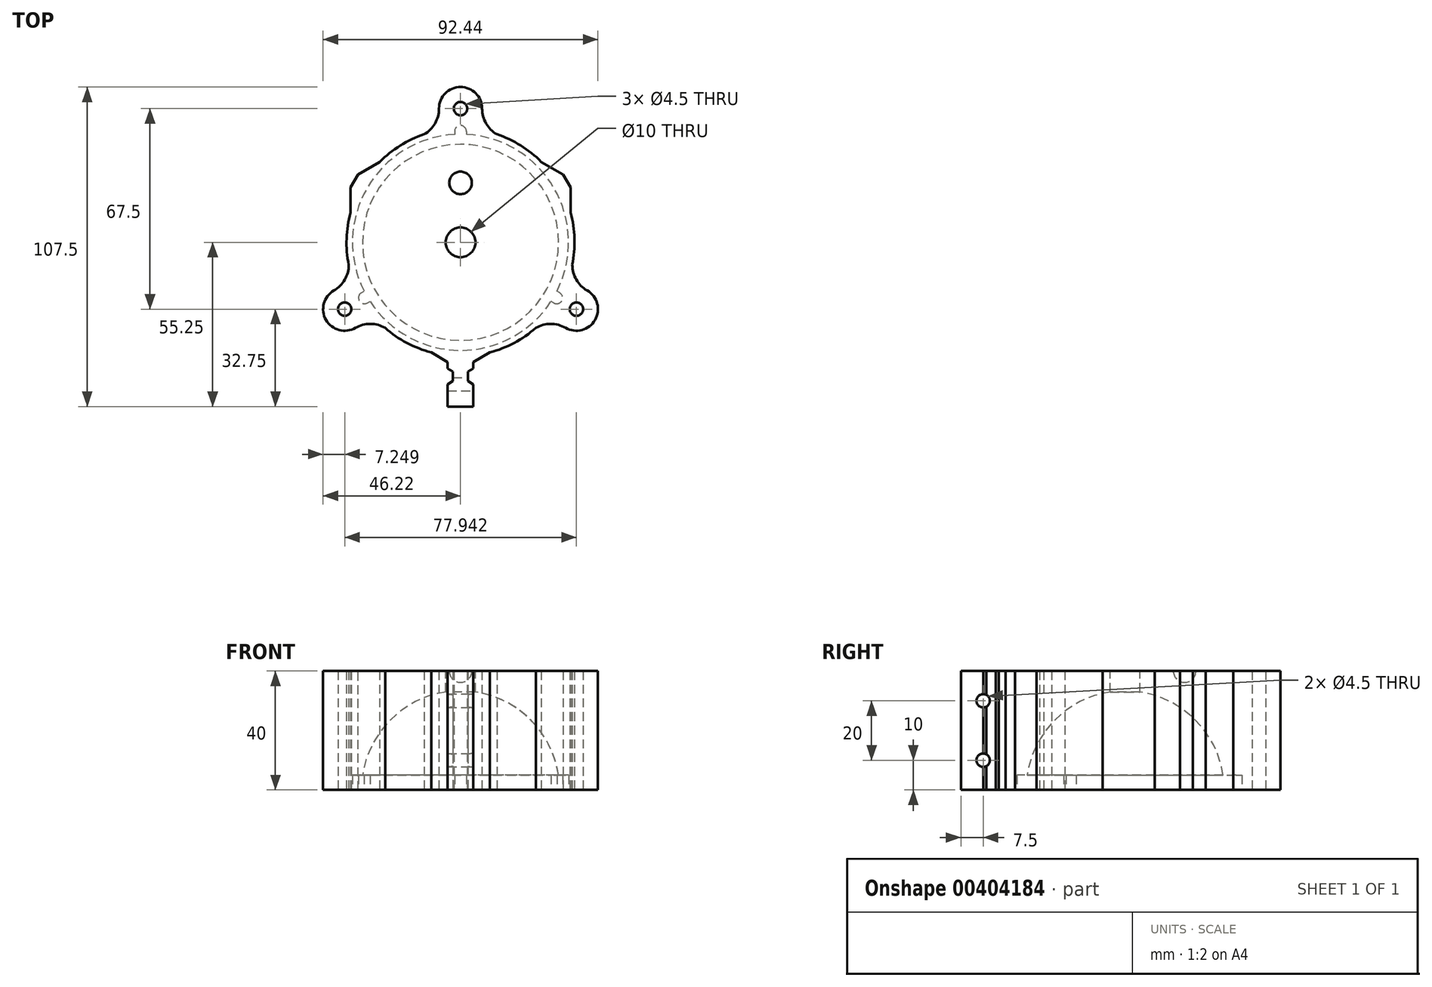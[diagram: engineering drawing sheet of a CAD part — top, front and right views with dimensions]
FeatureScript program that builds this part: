
annotation { "Feature Type Name" : "Feature", "Feature Type Description" : "" }
export const myFeature = defineFeature(function(context is Context, id is Id, definition is map)
    precondition{}
    {
        {
            var Q0;
            Q0=qCreatedBy(makeId("Top.planeOp"),FACE);
            var sketch = newSketch(context, id + "F0", { "sketchPlane" : qUnion([Q0])});
            skCircle(sketch, "E0", {"center": v(0, 0) * mm, "radius": 33.35 * mm});
            skCircle(sketch, "E1", {"center": v(0, 45) * mm, "radius": 2.25 * mm});
            skCircle(sketch, "E2", {"center": v(38.97, -22.5) * mm, "radius": 2.25 * mm});
            skCircle(sketch, "E3", {"center": v(-38.97, -22.5) * mm, "radius": 2.25 * mm});
            skArc(sketch, "E4", {"start": v(-25.35, -28.78) * mm, "mid": v(0, -38.35) * mm, "end": v(25.35, -28.78) * mm});
            skLineSegment(sketch, "E5", {"start": v(0, 0) * mm, "end": v(38.97, -22.5) * mm, "construction": true});
            skLineSegment(sketch, "E6", {"start": v(-38.97, -22.5) * mm, "end": v(0, 0) * mm, "construction": true});
            skArc(sketch, "E7", {"start": v(7.25, 45) * mm, "mid": v(0, 52.25) * mm, "end": v(-7.25, 45) * mm});
            skArc(sketch, "E8.1.0", {"start": v(-42.6, -16.22) * mm, "mid": v(-45.25, -26.12) * mm, "end": v(-35.35, -28.78) * mm});
            skArc(sketch, "E8.2.0", {"start": v(35.35, -28.78) * mm, "mid": v(45.25, -26.12) * mm, "end": v(42.6, -16.22) * mm});
            skArc(sketch, "E9", {"start": v(-12.25, 36.34) * mm, "mid": v(-8.59, 40) * mm, "end": v(-7.25, 45) * mm});
            skArc(sketch, "E10.MirrorCS", {"start": v(12.25, 36.34) * mm, "mid": v(8.59, 40) * mm, "end": v(7.25, 45) * mm});
            skArc(sketch, "E11.1.0", {"start": v(-25.35, -28.78) * mm, "mid": v(-30.35, -27.44) * mm, "end": v(-35.35, -28.78) * mm});
            skArc(sketch, "E11.1.1", {"start": v(-37.6, -7.57) * mm, "mid": v(-38.94, -12.56) * mm, "end": v(-42.6, -16.22) * mm});
            skArc(sketch, "E11.2.0", {"start": v(37.6, -7.57) * mm, "mid": v(38.94, -12.56) * mm, "end": v(42.6, -16.22) * mm});
            skArc(sketch, "E11.2.1", {"start": v(25.35, -28.78) * mm, "mid": v(30.35, -27.44) * mm, "end": v(35.35, -28.78) * mm});
            skArc(sketch, "E12.trimOffspring", {"start": v(37.6, -7.57) * mm, "mid": v(33.21, 19.18) * mm, "end": v(12.25, 36.34) * mm});
            skArc(sketch, "E13.trimOffspring", {"start": v(-12.25, 36.34) * mm, "mid": v(-33.21, 19.17) * mm, "end": v(-37.6, -7.57) * mm});
            skSolve(sketch);
        }
        {
            var Q0;
            Q0=qSketchRegion(id+"F0",true);
            extrude(context, id + "F1", {"entities" : qUnion([Q0]), "depth" : 40 * mm});
        }
        {
            var Q0;
            Q0=qCreatedBy(makeId("Top.planeOp"),FACE);
            var sketch = newSketch(context, id + "F2", { "sketchPlane" : qUnion([Q0])});
            skCircle(sketch, "E14.cCircle", {"center": v(0, 0) * mm, "radius": 37.02 * mm, "construction": true});
            skLineSegment(sketch, "E14.0", {"start": v(37.02, 21.37) * mm, "end": v(37.02, -21.37) * mm});
            skLineSegment(sketch, "E14.1", {"start": v(37.02, -21.37) * mm, "end": v(0, -42.75) * mm});
            skLineSegment(sketch, "E14.2", {"start": v(0, -42.75) * mm, "end": v(-37.02, -21.37) * mm});
            skLineSegment(sketch, "E14.3", {"start": v(-37.02, -21.37) * mm, "end": v(-37.02, 21.37) * mm});
            skLineSegment(sketch, "E14.4", {"start": v(-37.02, 21.37) * mm, "end": v(0, 42.75) * mm});
            skLineSegment(sketch, "E14.5", {"start": v(0, 42.75) * mm, "end": v(37.02, 21.38) * mm});
            skPoint(sketch, "E14.0.midPoint", {"position": v(37.02, 0) * mm});
            skCircle(sketch, "E15", {"center": v(0, 0) * mm, "radius": 33.35 * mm});
            skSolve(sketch);
        }
        {
            var Q0;
            Q0=qSketchRegion(id+"F2",true);
            extrude(context, id + "F3", {"entities" : qUnion([Q0]), "operationType" : NewBodyOperationType.ADD, "depth" : 40 * mm});
        }
        {
            var Q0;
            Q0=qCreatedBy(makeId("Top.planeOp"),FACE);
            var sketch = newSketch(context, id + "F4", { "sketchPlane" : qUnion([Q0])});
            skArc(sketch, "E16", {"start": v(-30.43, -19.88) * mm, "mid": v(0, -36.35) * mm, "end": v(30.43, -19.88) * mm});
            skArc(sketch, "E17", {"start": v(2, 37.32) * mm, "mid": v(0, 39.32) * mm, "end": v(-2, 37.32) * mm});
            skLineSegment(sketch, "E18", {"start": v(-2, 37.32) * mm, "end": v(-2, 36.3) * mm});
            skLineSegment(sketch, "E19.MirrorCS", {"start": v(2, 37.32) * mm, "end": v(2, 36.3) * mm});
            skLineSegment(sketch, "E20.1.0", {"start": v(-33.32, -16.93) * mm, "end": v(-32.43, -16.42) * mm});
            skArc(sketch, "E20.1.1", {"start": v(-33.32, -16.93) * mm, "mid": v(-34.05, -19.66) * mm, "end": v(-31.32, -20.4) * mm});
            skLineSegment(sketch, "E20.1.2", {"start": v(-31.32, -20.4) * mm, "end": v(-30.43, -19.88) * mm});
            skLineSegment(sketch, "E20.2.0", {"start": v(31.32, -20.4) * mm, "end": v(30.43, -19.88) * mm});
            skArc(sketch, "E20.2.1", {"start": v(31.32, -20.4) * mm, "mid": v(34.05, -19.66) * mm, "end": v(33.32, -16.93) * mm});
            skLineSegment(sketch, "E20.2.2", {"start": v(33.32, -16.93) * mm, "end": v(32.43, -16.42) * mm});
            skArc(sketch, "E21.trimOffspring", {"start": v(32.43, -16.42) * mm, "mid": v(31.48, 18.18) * mm, "end": v(2, 36.3) * mm});
            skArc(sketch, "E22.trimOffspring", {"start": v(-2, 36.3) * mm, "mid": v(-31.48, 18.17) * mm, "end": v(-32.43, -16.42) * mm});
            skSolve(sketch);
        }
        {
            var Q0;
            Q0=qSketchRegion(id+"F4",true);
            extrude(context, id + "F5", {"entities" : qUnion([Q0]), "operationType" : NewBodyOperationType.REMOVE, "depth" : 5 * mm});
        }
        {
            var Q0;
            Q0=makeQuery(id+"F3.boolean.opBoolean","MERGE",FACE,{"derivedFrom":[makeQuery(id+"F1.opExtrude","CAP_FACE",FACE,{"disambiguationData":[OSD([sQuery(id+"F0.wireOp",EDGE,"E0"),sQuery(id+"F0.wireOp",EDGE,"E1"),sQuery(id+"F0.wireOp",EDGE,"E2"),sQuery(id+"F0.wireOp",EDGE,"E3"),sQuery(id+"F0.wireOp",EDGE,"E4"),sQuery(id+"F0.wireOp",EDGE,"E7"),sQuery(id+"F0.wireOp",EDGE,"E8.1.0"),sQuery(id+"F0.wireOp",EDGE,"E8.2.0"),sQuery(id+"F0.wireOp",EDGE,"E9"),sQuery(id+"F0.wireOp",EDGE,"E10.MirrorCS"),sQuery(id+"F0.wireOp",EDGE,"E11.1.0"),sQuery(id+"F0.wireOp",EDGE,"E11.1.1"),sQuery(id+"F0.wireOp",EDGE,"E11.2.0"),sQuery(id+"F0.wireOp",EDGE,"E11.2.1"),sQuery(id+"F0.wireOp",EDGE,"E12.trimOffspring"),sQuery(id+"F0.wireOp",EDGE,"E13.trimOffspring")])],"isStart":false}),makeQuery(id+"F3.opExtrude","CAP_FACE",FACE,{"disambiguationData":[OSD([sQuery(id+"F2.wireOp",EDGE,"E14.0"),sQuery(id+"F2.wireOp",EDGE,"E14.1"),sQuery(id+"F2.wireOp",EDGE,"E14.2"),sQuery(id+"F2.wireOp",EDGE,"E14.3"),sQuery(id+"F2.wireOp",EDGE,"E14.4"),sQuery(id+"F2.wireOp",EDGE,"E14.5"),sQuery(id+"F2.wireOp",EDGE,"E15")])],"isStart":false})]});
            var sketch = newSketch(context, id + "F6", { "sketchPlane" : qUnion([Q0])});
            skCircle(sketch, "E23.cCircle", {"center": v(0, 0) * mm, "radius": 37.02 * mm, "construction": true});
            skLineSegment(sketch, "E23.0", {"start": v(37.02, 21.37) * mm, "end": v(37.02, -21.38) * mm});
            skLineSegment(sketch, "E23.1", {"start": v(37.02, -21.37) * mm, "end": v(0, -42.75) * mm});
            skLineSegment(sketch, "E23.2", {"start": v(0, -42.75) * mm, "end": v(-37.02, -21.38) * mm});
            skLineSegment(sketch, "E23.3", {"start": v(-37.02, -21.37) * mm, "end": v(-37.02, 21.37) * mm});
            skLineSegment(sketch, "E23.4", {"start": v(-37.02, 21.37) * mm, "end": v(0, 42.75) * mm});
            skLineSegment(sketch, "E23.5", {"start": v(0, 42.75) * mm, "end": v(37.02, 21.38) * mm});
            skPoint(sketch, "E23.0.midPoint", {"position": v(37.02, 0) * mm});
            skCircle(sketch, "E24", {"center": v(0, 0) * mm, "radius": 5 * mm});
            skSolve(sketch);
        }
        {
            var Q0;
            Q0 = qSketchRegion(id + "F6", true);
            extrude(context, id + "F7", {"entities" : qUnion([Q0]), "operationType" : NewBodyOperationType.ADD, "oppositeDirection" : true, "depth" : 6 * mm});
        }
        {
            var Q0;
            Q0=qCreatedBy(makeId("Front.planeOp"),FACE);
            var sketch = newSketch(context, id + "F8", { "sketchPlane" : qUnion([Q0])});
            skArc(sketch, "E25", {"start": v(32.97, 5) * mm, "mid": v(23.58, 23.58) * mm, "end": v(5, 32.97) * mm});
            skLineSegment(sketch, "E26", {"start": v(5, 32.97) * mm, "end": v(5, 34) * mm});
            skLineSegment(sketch, "E27", {"start": v(5, 34) * mm, "end": v(38.33, 34) * mm});
            skLineSegment(sketch, "E28", {"start": v(38.33, 34) * mm, "end": v(38.33, 5) * mm});
            skLineSegment(sketch, "E29", {"start": v(38.33, 0) * mm, "end": v(33.35, 0) * mm, "construction": true});
            skLineSegment(sketch, "E30", {"start": v(32.97, 5) * mm, "end": v(38.33, 5) * mm});
            skLineSegment(sketch, "E31", {"start": v(0, 40) * mm, "end": v(0, 0) * mm, "construction": true});
            skSolve(sketch);
        }
        {
            var Q0;
            Q0 = qSketchRegion(id + "F8", true);
            var Q1;
            Q1=sQuery(id+"F8.wireOp",EDGE,"E31");
            revolve(context, id + "F9", {"operationType" : NewBodyOperationType.ADD, "entities" : qUnion([Q0]), "axis" : qUnion([Q1]), "revolveType" : RevolveType.FULL});
        }
        {
            var Q0;
            Q0=makeQuery(id+"F7.boolean.opBoolean","MERGE",FACE,{"derivedFrom":[makeQuery(id+"F3.boolean.opBoolean","MERGE",FACE,{"derivedFrom":[makeQuery(id+"F1.opExtrude","CAP_FACE",FACE,{"disambiguationData":[OSD([sQuery(id+"F0.wireOp",EDGE,"E0"),sQuery(id+"F0.wireOp",EDGE,"E1"),sQuery(id+"F0.wireOp",EDGE,"E2"),sQuery(id+"F0.wireOp",EDGE,"E3"),sQuery(id+"F0.wireOp",EDGE,"E4"),sQuery(id+"F0.wireOp",EDGE,"E7"),sQuery(id+"F0.wireOp",EDGE,"E8.1.0"),sQuery(id+"F0.wireOp",EDGE,"E8.2.0"),sQuery(id+"F0.wireOp",EDGE,"E9"),sQuery(id+"F0.wireOp",EDGE,"E10.MirrorCS"),sQuery(id+"F0.wireOp",EDGE,"E11.1.0"),sQuery(id+"F0.wireOp",EDGE,"E11.1.1"),sQuery(id+"F0.wireOp",EDGE,"E11.2.0"),sQuery(id+"F0.wireOp",EDGE,"E11.2.1"),sQuery(id+"F0.wireOp",EDGE,"E12.trimOffspring"),sQuery(id+"F0.wireOp",EDGE,"E13.trimOffspring")])],"isStart":false}),makeQuery(id+"F3.opExtrude","CAP_FACE",FACE,{"disambiguationData":[OSD([sQuery(id+"F2.wireOp",EDGE,"E14.0"),sQuery(id+"F2.wireOp",EDGE,"E14.1"),sQuery(id+"F2.wireOp",EDGE,"E14.2"),sQuery(id+"F2.wireOp",EDGE,"E14.3"),sQuery(id+"F2.wireOp",EDGE,"E14.4"),sQuery(id+"F2.wireOp",EDGE,"E14.5"),sQuery(id+"F2.wireOp",EDGE,"E15")])],"isStart":false})]}),makeQuery(id+"F7.opExtrude","CAP_FACE",FACE,{"disambiguationData":[OSD([sQuery(id+"F6.wireOp",EDGE,"E23.0"),sQuery(id+"F6.wireOp",EDGE,"E23.1"),sQuery(id+"F6.wireOp",EDGE,"E23.2"),sQuery(id+"F6.wireOp",EDGE,"E23.3"),sQuery(id+"F6.wireOp",EDGE,"E23.4"),sQuery(id+"F6.wireOp",EDGE,"E23.5"),sQuery(id+"F6.wireOp",EDGE,"E24")])],"isStart":true})]});
            var sketch = newSketch(context, id + "F10", { "sketchPlane" : qUnion([Q0])});
            skArc(sketch, "E32", {"start": v(0, 23.8) * mm, "mid": v(3.8, 20) * mm, "end": v(0, 16.2) * mm});
            skLineSegment(sketch, "E33", {"start": v(0, 23.8) * mm, "end": v(0, 16.2) * mm});
            skSolve(sketch);
        }
        {
            var Q0;
            Q0 = qSketchRegion(id + "F10", true);
            var Q1;
            Q1=sQuery(id+"F10.wireOp",EDGE,"E33");
            revolve(context, id + "F11", {"operationType" : NewBodyOperationType.REMOVE, "entities" : qUnion([Q0]), "axis" : qUnion([Q1]), "revolveType" : RevolveType.FULL, "oppositeDirection" : true});
        }
        {
            var Q0;
            Q0=makeQuery(id+"F3.opExtrude","SWEPT_EDGE",EDGE,{"disambiguationData":[OSD([sQuery(id+"F2.wireOp",EDGE,"E14.3"),sQuery(id+"F2.wireOp",EDGE,"E14.4")])]});
            var Q1;
            Q1=makeQuery(id+"F3.opExtrude","SWEPT_EDGE",EDGE,{"disambiguationData":[OSD([sQuery(id+"F2.wireOp",EDGE,"E14.1"),sQuery(id+"F2.wireOp",EDGE,"E14.2")])]});
            var Q2;
            Q2=makeQuery(id+"F3.opExtrude","SWEPT_EDGE",EDGE,{"disambiguationData":[OSD([sQuery(id+"F2.wireOp",EDGE,"E14.0"),sQuery(id+"F2.wireOp",EDGE,"E14.5")])]});
            chamfer(context, id + "F12", {"entities" : qUnion([Q0, Q1, Q2]), "width" : 5 * mm, "tangentPropagation" : true});
        }
        {
            var Q0;
            Q0=qCreatedBy(makeId("Top.planeOp"),FACE);
            var sketch = newSketch(context, id + "F13", { "sketchPlane" : qUnion([Q0])});
            skLineSegment(sketch, "E34", {"start": v(0, -40.25) * mm, "end": v(4.33, -40.25) * mm});
            skLineSegment(sketch, "E35", {"start": v(4.33, -40.25) * mm, "end": v(4.33, -42.47) * mm});
            skLineSegment(sketch, "E36", {"start": v(4.33, -55.25) * mm, "end": v(0, -55.25) * mm});
            skLineSegment(sketch, "E37.MirrorCS", {"start": v(-4.33, -40.25) * mm, "end": v(-4.33, -42.47) * mm});
            skLineSegment(sketch, "E38.MirrorCS", {"start": v(0, -40.25) * mm, "end": v(-4.33, -40.25) * mm});
            skLineSegment(sketch, "E39.MirrorCS", {"start": v(-4.33, -55.25) * mm, "end": v(0, -55.25) * mm});
            skLineSegment(sketch, "E40", {"start": v(-4.33, -47.75) * mm, "end": v(-2.53, -46.71) * mm});
            skLineSegment(sketch, "E41", {"start": v(-2.53, -46.71) * mm, "end": v(-2.53, -43.51) * mm});
            skLineSegment(sketch, "E42", {"start": v(-2.53, -43.51) * mm, "end": v(-4.33, -42.47) * mm});
            skLineSegment(sketch, "E43.MirrorCS", {"start": v(2.53, -43.51) * mm, "end": v(4.33, -42.47) * mm});
            skLineSegment(sketch, "E44.MirrorCS", {"start": v(2.53, -46.71) * mm, "end": v(2.53, -43.51) * mm});
            skLineSegment(sketch, "E45.MirrorCS", {"start": v(4.33, -47.75) * mm, "end": v(2.53, -46.71) * mm});
            skLineSegment(sketch, "E46.trimOffspring", {"start": v(-4.33, -47.75) * mm, "end": v(-4.33, -55.25) * mm});
            skLineSegment(sketch, "E47.trimOffspring", {"start": v(4.33, -47.75) * mm, "end": v(4.33, -55.25) * mm});
            skSolve(sketch);
        }
        {
            var Q0;
            Q0 = qSketchRegion(id + "F13", true);
            extrude(context, id + "F14", {"entities" : qUnion([Q0]), "operationType" : NewBodyOperationType.ADD, "depth" : 40 * mm});
        }
        {
            var Q0;
            Q0=makeQuery(id+"F14.opExtrude","SWEPT_FACE",FACE,{"disambiguationData":[OSD([sQuery(id+"F13.wireOp",EDGE,"E47.trimOffspring")])]});
            var sketch = newSketch(context, id + "F15", { "sketchPlane" : qUnion([Q0])});
            skCircle(sketch, "E48", {"center": v(-47.75, 10) * mm, "radius": 2.25 * mm});
            skCircle(sketch, "E49", {"center": v(-47.75, 30) * mm, "radius": 2.25 * mm});
            skSolve(sketch);
        }
        {
            var Q0;
            Q0 = qSketchRegion(id + "F15", true);
            extrude(context, id + "F16", {"entities" : qUnion([Q0]), "operationType" : NewBodyOperationType.REMOVE, "endBound" : BoundingType.THROUGH_ALL, "oppositeDirection" : true, "depth" : 25 * mm});
        }
    });
